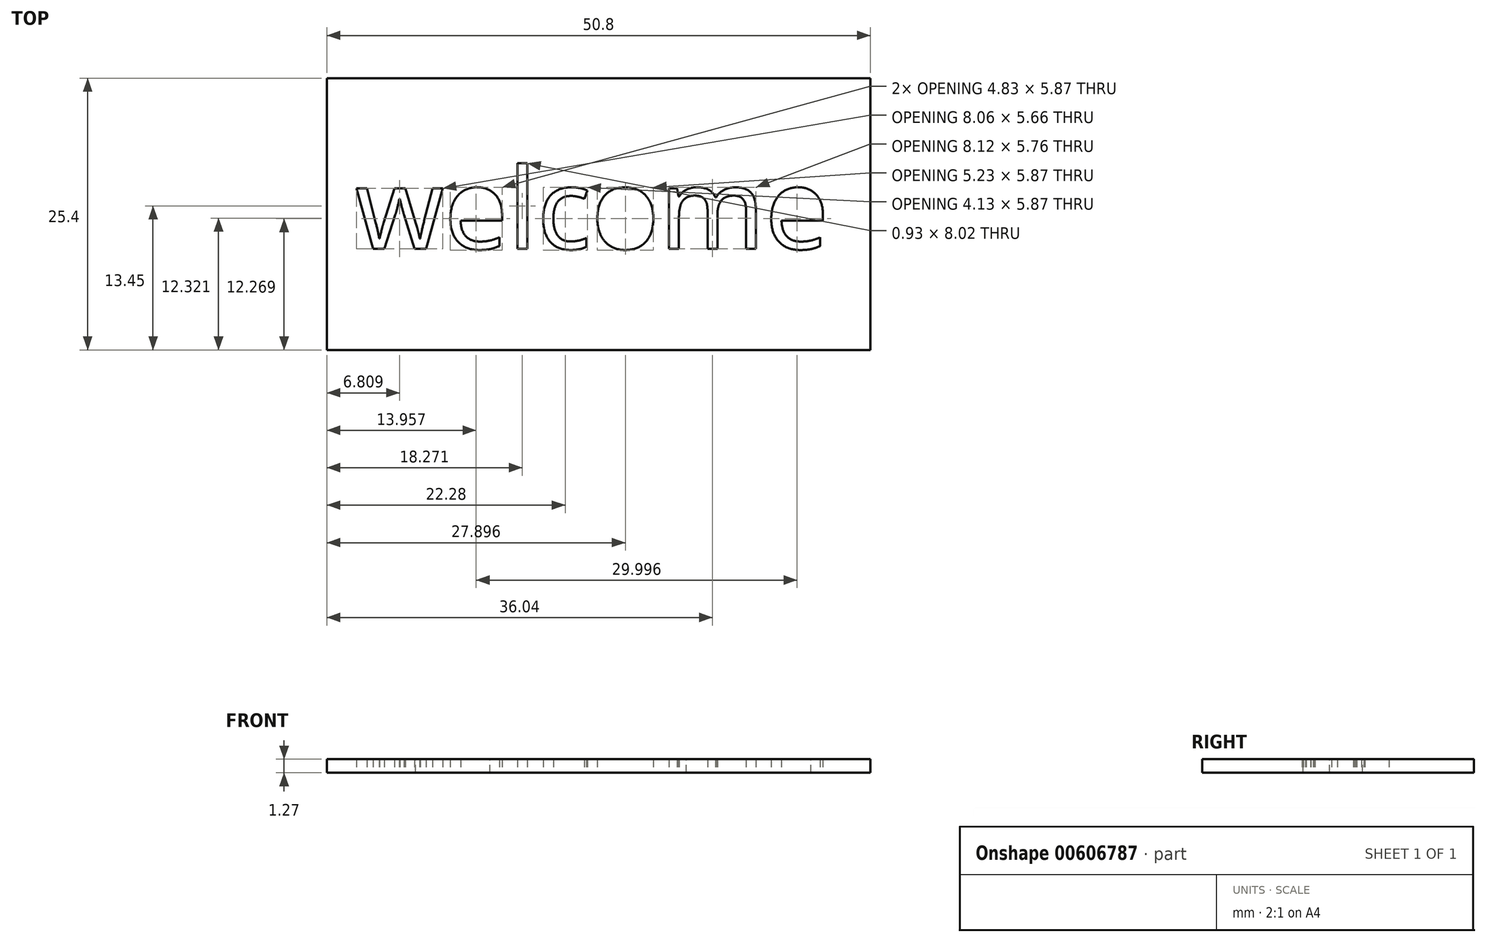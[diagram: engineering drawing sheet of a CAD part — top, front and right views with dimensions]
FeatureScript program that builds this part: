
annotation { "Feature Type Name" : "Feature", "Feature Type Description" : "" }
export const myFeature = defineFeature(function(context is Context, id is Id, definition is map)
    precondition{}
    {
        {
            var Q0;
            Q0=qCreatedBy(makeId("Top.planeOp"),FACE);
            var sketch = newSketch(context, id + "F0", { "sketchPlane" : qUnion([Q0])});
            skLineSegment(sketch, "E0.bottom", {"start": v(-23.82, 13.44) * mm, "end": v(26.98, 13.44) * mm});
            skLineSegment(sketch, "E0.top", {"start": v(-23.82, -11.96) * mm, "end": v(26.98, -11.96) * mm});
            skLineSegment(sketch, "E0.left", {"start": v(-23.82, 13.44) * mm, "end": v(-23.82, -11.96) * mm});
            skLineSegment(sketch, "E0.right", {"start": v(26.98, 13.44) * mm, "end": v(26.98, -11.96) * mm});
            skText(sketch, "E1", { "text": "welcome", "fontName": "NotoSans-Regular.ttf"});
            const initialGuessF0  = {"E1": [-0.02116, -0.00252, 1, 0, 0.0076]};
            skSetInitialGuess(sketch, initialGuessF0);
            skSolve(sketch);
        }
        {
            var Q0;
            Q0 = qSketchRegion(id + "F0", true);
            extrude(context, id + "F1", {"entities" : qUnion([Q0]), "depth" : 1.27 * mm, "offsetDistance" : 25.4 * mm});
        }
    });
